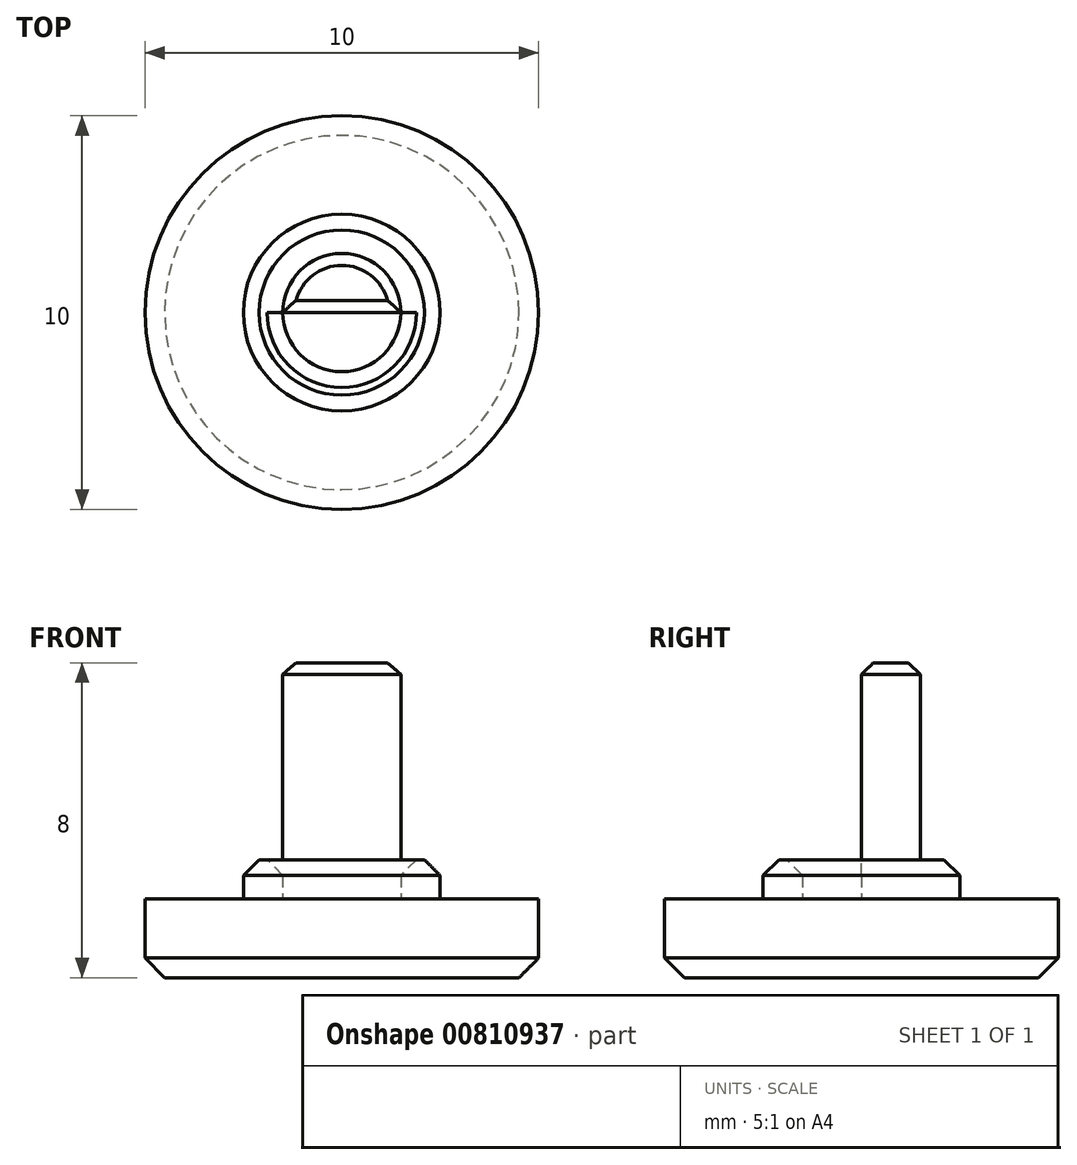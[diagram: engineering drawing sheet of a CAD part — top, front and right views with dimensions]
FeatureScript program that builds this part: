
annotation { "Feature Type Name" : "Feature", "Feature Type Description" : "" }
export const myFeature = defineFeature(function(context is Context, id is Id, definition is map)
    precondition{}
    {
        {
            assignVariable(context, id + "F0", {"name" : "Long", "anyValue" : 8});
        }
        {
            var Q0;
            Q0=qCreatedBy(makeId("Top.planeOp"),FACE);
            var sketch = newSketch(context, id + "F1", { "sketchPlane" : qUnion([Q0])});
            skCircle(sketch, "E0", {"center": v(0, 0) * mm, "radius": 1.5 * mm});
            skCircle(sketch, "E1", {"center": v(0, 0) * mm, "radius": 2.5 * mm});
            skCircle(sketch, "E2", {"center": v(0, 0) * mm, "radius": 5 * mm});
            skLineSegment(sketch, "E3", {"start": v(-1.5, 0) * mm, "end": v(1.5, 0) * mm});
            skSolve(sketch);
        }
        {
            var Q0;
            {var subQ0=sQuery(id+"F1.wireOp",EDGE,"E3");Q0=makeQuery(id+"F1.imprint","IMPRINT",FACE,{"disambiguationData":[TD([[makeQuery(id+"F1.imprint","IMPRINT",EDGE,{"derivedFrom":subQ0}),1.0]])]});}
            extrude(context, id + "F2", {"entities" : qUnion([Q0]), "depth" : (getVariable(context, 'Long')) * mm, "offsetDistance" : 25 * mm});
        }
        {
            assignVariable(context, id + "F3", {"name" : "Rebord", "anyValue" : 3});
        }
        {
            var Q0;
            Q0=makeQuery(id+"F1.imprint","IMPRINT",FACE,{"disambiguationData":[TD([[makeQuery(id+"F1.imprint","IMPRINT",EDGE,{"derivedFrom":sQuery(id+"F1.wireOp",EDGE,"E1")}),1.0]])]});
            extrude(context, id + "F4", {"entities" : qUnion([Q0]), "operationType" : NewBodyOperationType.ADD, "depth" : (getVariable(context, 'Rebord')) * mm, "offsetDistance" : 25 * mm});
        }
        {
            assignVariable(context, id + "F5", {"name" : "Bouton", "anyValue" : 2});
        }
        {
            var Q0;
            Q0=qSketchRegion(id+"F1",true);
            extrude(context, id + "F6", {"entities" : qUnion([Q0]), "operationType" : NewBodyOperationType.ADD, "depth" : (getVariable(context, 'Bouton')) * mm, "offsetDistance" : 25 * mm});
        }
        {
            var Q0;
            {var subQ0=sQuery(id+"F1.wireOp",EDGE,"E3");Q0=makeQuery(id+"F1.imprint","IMPRINT",FACE,{"disambiguationData":[TD([[makeQuery(id+"F1.imprint","IMPRINT",EDGE,{"derivedFrom":subQ0}),-1.0]])]});}
            extrude(context, id + "F7", {"entities" : qUnion([Q0]), "operationType" : NewBodyOperationType.ADD, "depth" : 2 * mm, "offsetDistance" : 25 * mm});
        }
        {
            var Q0;
            Q0=makeQuery(id+"F4.opExtrude","CAP_EDGE",EDGE,{"disambiguationData":[OSD([sQuery(id+"F1.wireOp",EDGE,"E1")])],"isStart":false});
            chamfer(context, id + "F8", {"entities" : qUnion([Q0]), "width" : 0.4 * mm, "tangentPropagation" : true});
        }
        {
            var Q0;
            Q0=makeQuery(id+"F2.opExtrude","CAP_EDGE",EDGE,{"disambiguationData":[OSD([sQuery(id+"F1.wireOp",EDGE,"E0")])],"isStart":false});
            var Q1;
            Q1=makeQuery(id+"F2.opExtrude","CAP_EDGE",EDGE,{"disambiguationData":[OSD([sQuery(id+"F1.wireOp",EDGE,"E3")])],"isStart":false});
            chamfer(context, id + "F9", {"entities" : qUnion([Q0, Q1]), "width" : 0.3 * mm, "tangentPropagation" : true});
        }
        {
            var Q0;
            Q0=makeQuery(id+"F6.opExtrude","CAP_EDGE",EDGE,{"disambiguationData":[OSD([sQuery(id+"F1.wireOp",EDGE,"E2")])],"isStart":true});
            chamfer(context, id + "F10", {"entities" : qUnion([Q0]), "width" : 0.5 * mm, "tangentPropagation" : true});
        }
        {
            var Q0;
            {var subQ0=sQuery(id+"F1.wireOp",EDGE,"E0");Q0=makeQuery(id+"F4.boolean.opBoolean","SPLIT",EDGE,{"disambiguationData":[topologyDisambiguationEdgeConnected([makeQuery(id+"F4.opExtrude","SWEPT_FACE",FACE,{"disambiguationData":[OSD([subQ0])]})])],"derivedFrom":makeQuery(id+"F4.opExtrude","CAP_EDGE",EDGE,{"disambiguationData":[OSD([subQ0])],"isStart":false})});}
            chamfer(context, id + "F11", {"entities" : qUnion([Q0]), "width" : 0.4 * mm, "tangentPropagation" : true});
        }
    });
